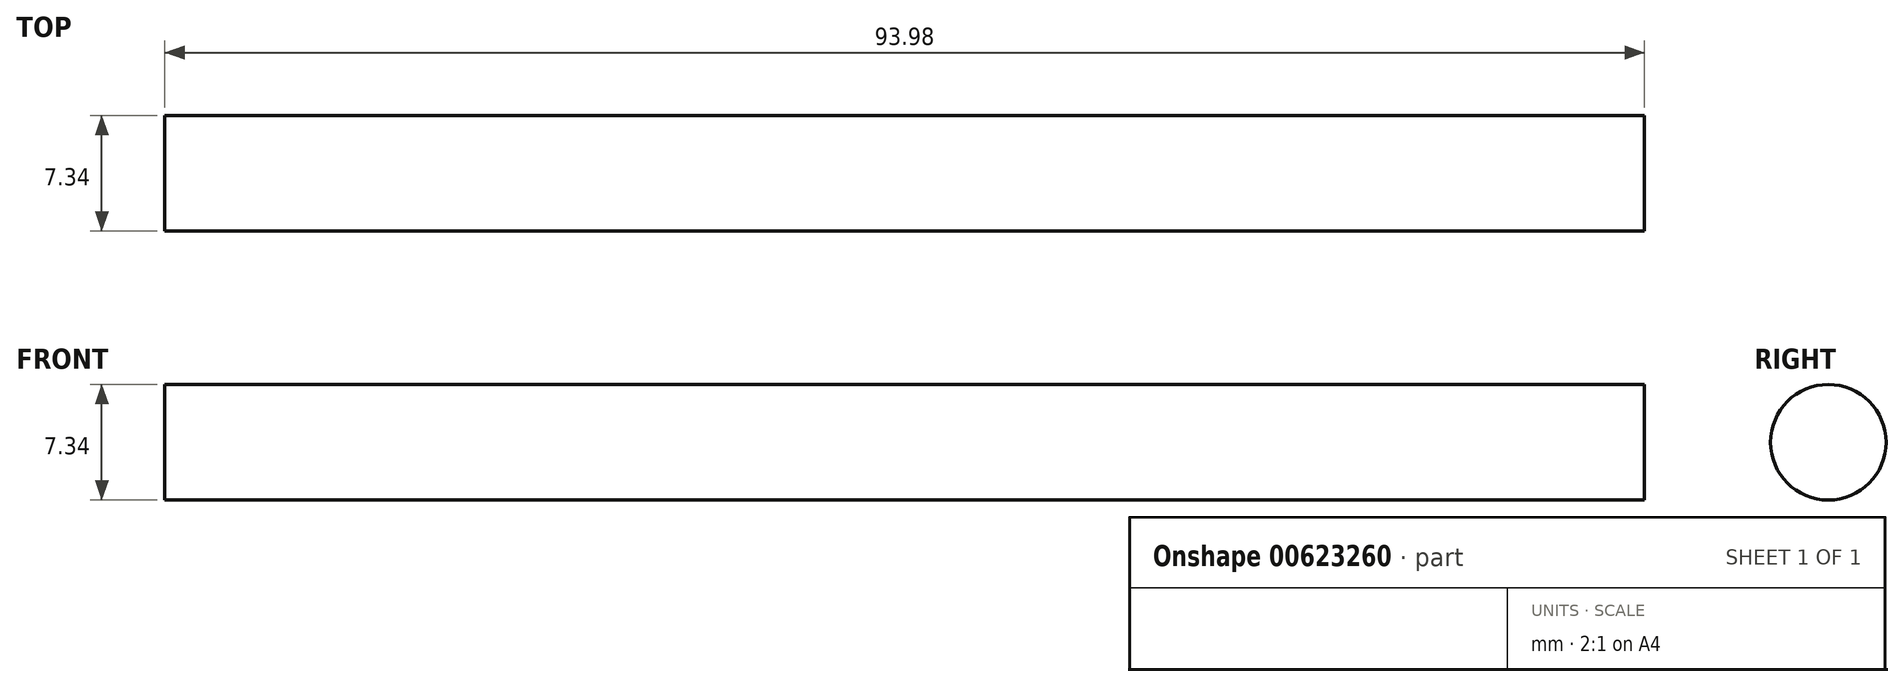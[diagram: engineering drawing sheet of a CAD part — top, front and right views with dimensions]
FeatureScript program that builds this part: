
annotation { "Feature Type Name" : "Feature", "Feature Type Description" : "" }
export const myFeature = defineFeature(function(context is Context, id is Id, definition is map)
    precondition{}
    {
        {
            var Q0;
            Q0=qCreatedBy(makeId("Right.planeOp"),FACE);
            var sketch = newSketch(context, id + "F0", { "sketchPlane" : qUnion([Q0])});
            skCircle(sketch, "E0", {"center": v(0, 0) * mm, "radius": 3.67 * mm});
            skSolve(sketch);
        }
        {
            var Q0;
            Q0=qSketchRegion(id+"F0",true);
            extrude(context, id + "F1", {"entities" : qUnion([Q0]), "depth" : 93.98 * mm, "offsetDistance" : 25.4 * mm});
        }
    });
